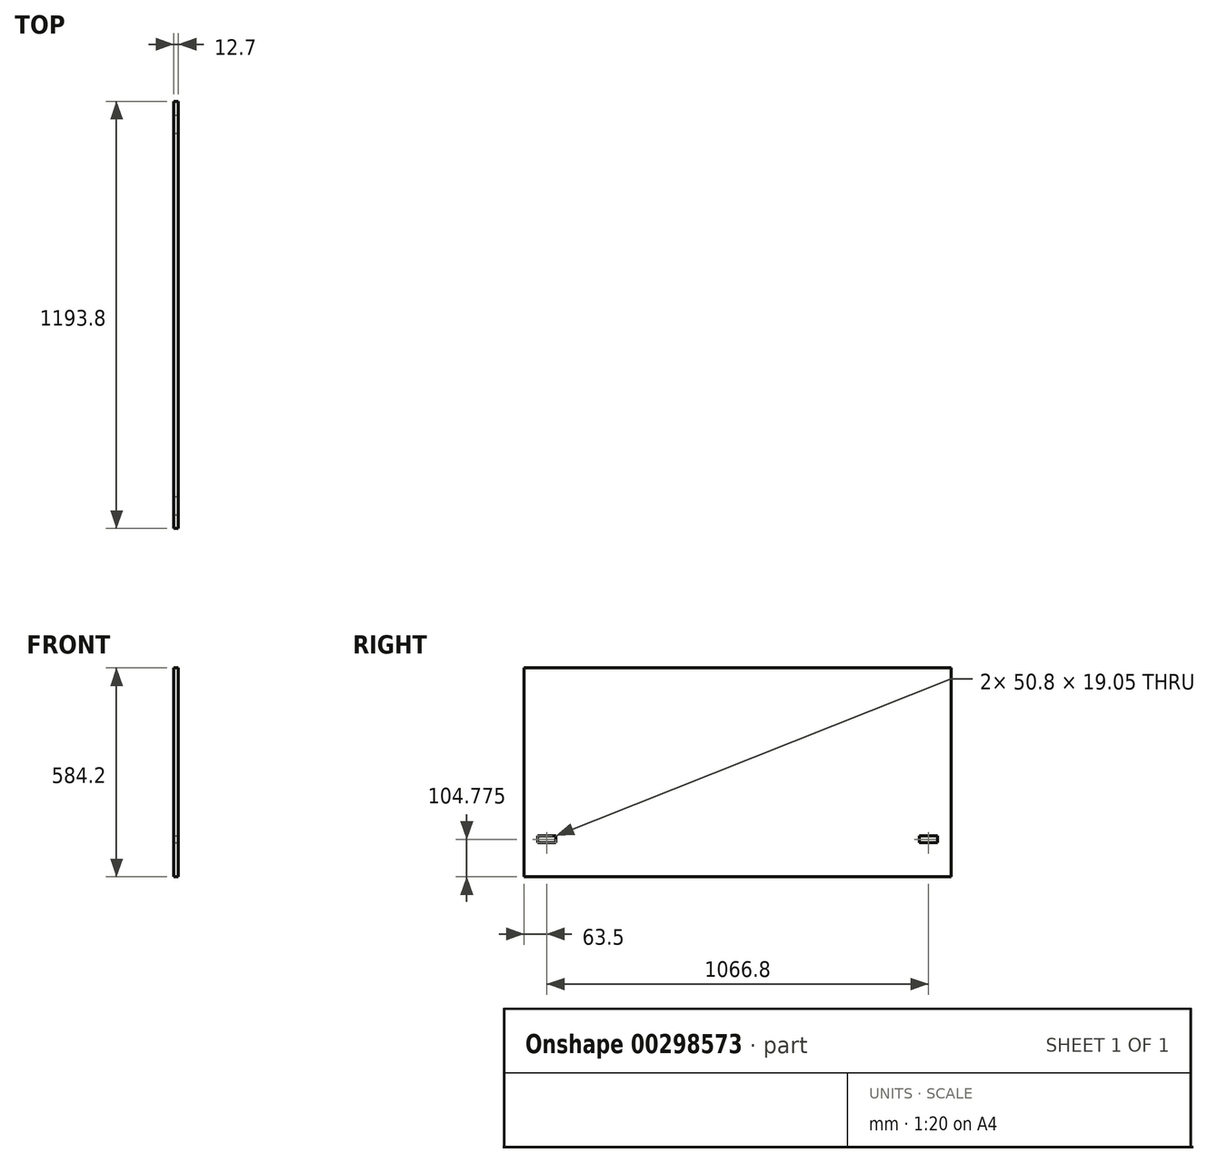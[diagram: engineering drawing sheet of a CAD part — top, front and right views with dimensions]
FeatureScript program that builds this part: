
annotation { "Feature Type Name" : "Feature", "Feature Type Description" : "" }
export const myFeature = defineFeature(function(context is Context, id is Id, definition is map)
    precondition{}
    {
        {
            assignVariable(context, id + "F0", {"name" : "thickness", "anyValue" : 12.7 * mm});
        }
        {
            var Q0;
            Q0=qCreatedBy(makeId("Right.planeOp"),FACE);
            var sketch = newSketch(context, id + "F1", { "sketchPlane" : qUnion([Q0])});
            skLineSegment(sketch, "E0", {"start": v(0, 0) * mm, "end": v(-596.9, 0) * mm});
            skLineSegment(sketch, "E1", {"start": v(-596.9, 584.2) * mm, "end": v(0, 584.2) * mm});
            skLineSegment(sketch, "E2", {"start": v(0, 584.2) * mm, "end": v(0, 0) * mm});
            skLineSegment(sketch, "E3", {"start": v(-596.9, 584.2) * mm, "end": v(-596.9, 0) * mm});
            skLineSegment(sketch, "E4", {"start": v(-508, 95.25) * mm, "end": v(-558.8, 95.25) * mm});
            skLineSegment(sketch, "E5", {"start": v(-558.8, 95.25) * mm, "end": v(-558.8, 114.3) * mm});
            skLineSegment(sketch, "E6", {"start": v(-558.8, 114.3) * mm, "end": v(-508, 114.3) * mm});
            skLineSegment(sketch, "E7", {"start": v(-508, 114.3) * mm, "end": v(-508, 95.25) * mm});
            skSolve(sketch);
        }
        {
            var Q0;
            Q0=qSketchRegion(id+"F1",true);
            extrude(context, id + "F2", {"entities" : qUnion([Q0]), "oppositeDirection" : true, "depth" : getVariable(context, 'thickness')});
        }
        {
            var Q0;
            Q0=makeQuery(id+"F2.opExtrude","SWEPT_BODY",BODY,{"disambiguationData":[OSD([sQuery(id+"F1.wireOp",EDGE,"E0"),sQuery(id+"F1.wireOp",EDGE,"3tMfJS4N-ypb9-l0Ta-9uWP-DEAdmuzVW53T"),sQuery(id+"F1.wireOp",EDGE,"jTk7peYf-2WaW-bSmY-uFjm-mRNM38bE61Lu"),sQuery(id+"F1.wireOp",EDGE,"8JaLhZk6-0cRP-R6hW-y9Vx-7hvVqPKNujpa"),sQuery(id+"F1.wireOp",EDGE,"TZnCuJOO-Qegh-hEIp-s20Q-fgZjGuWCg3vA"),sQuery(id+"F1.wireOp",EDGE,"tWWneQS6-UdGj-g5Fi-xo0S-2rr6tD82CQqT"),sQuery(id+"F1.wireOp",EDGE,"b8hwCOqo-nM54-PEK6-M3np-szgyElorNUvT"),sQuery(id+"F1.wireOp",EDGE,"7F31Xd9x-INzy-KnOs-3kYU-8WDCusqLbkJ0"),sQuery(id+"F1.wireOp",EDGE,"hYDcJfnw-XkOK-fOym-D8zb-R2Y2sOVZZuOK"),sQuery(id+"F1.wireOp",EDGE,"9lJIcL2o-SPeb-7oC6-sUFb-yPgbFpKkTIm6"),sQuery(id+"F1.wireOp",EDGE,"lioOfQHn-mJ2w-PqYM-xibh-QE0FSVLkZLlc"),sQuery(id+"F1.wireOp",EDGE,"yiOthWJt-mPfk-9UEe-1KvM-reueNEaVAevJ"),sQuery(id+"F1.wireOp",EDGE,"gPYPsZx8-Czem-Lv42-KuP6-J9U4XgOXf9pq"),sQuery(id+"F1.wireOp",EDGE,"UfnbemdW-929Q-INjx-RDmx-ac4GmVFYn7Om"),sQuery(id+"F1.wireOp",EDGE,"E1"),sQuery(id+"F1.wireOp",EDGE,"E2")])]});
            var Q1;
            Q1=qCreatedBy(makeId("Front.planeOp"),FACE);
            mirror(context, id + "F3", {"operationType" : NewBodyOperationType.ADD, "entities" : qUnion([Q0]), "mirrorPlane" : qUnion([Q1])});
        }
    });
